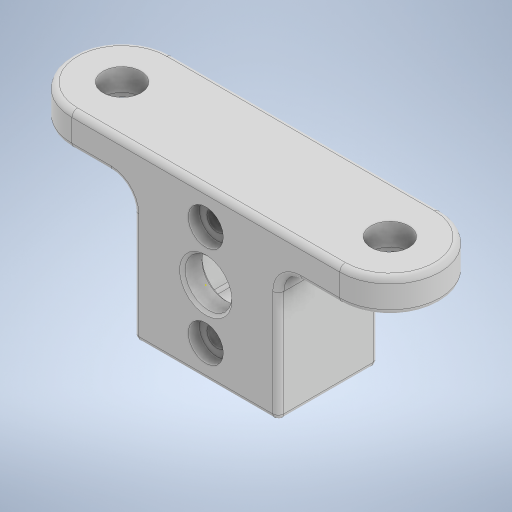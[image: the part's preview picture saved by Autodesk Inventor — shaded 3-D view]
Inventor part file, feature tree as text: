
AUTODESK INVENTOR PART (.ipt)
format: ipt  version: 2024.2 (Build 282272000, 272)  size: 382,464 bytes
history: native  units: mm
features: sketch x7, extrude x6, fillet x4, chamfer x1
ambient origin geometry x8: Origin, YZ Plane, XZ Plane, XY Plane, X Axis, Y Axis, Z Axis, Center Point
bodies: Solid1 (feature_tree)
feature tree (18):
  sketch  "Sketch1"  dims[d0=1.8mm d1=9.0mm]
  extrude  "Extrusion1"  Depth=9.0mm
  extrude  "Extrusion2"  Depth=4.5mm
  extrude  "Extrusion3"  Depth=15.0mm
  fillet  "Fillet1"  Radius=7.5mm
  fillet  "Fillet2"  Radius=6.5mm
  extrude  "Extrusion4"  Depth=1.5mm
  fillet  "Fillet3"  Radius=1.5mm
  fillet  "Fillet4"  Radius=1.5mm
  chamfer  "Chamfer1"  Distance=7.0mm
  extrude  "Extrusion5"  Depth=10.0mm
  extrude  "Extrusion6"  Depth=2.0mm
  sketch  "Sketch2"  dims[d2=4.195mm d3=4.5mm]
  sketch  "Sketch3"  dims[d4=13.0mm d5=15.0mm d6=7.5mm d7=6.5mm]
  sketch  "Sketch4"  dims[d8=2.0mm d9=0.0mm d10=1.5mm d11=1.5mm d12=1.5mm]
  sketch  "Sketch5"  dims[d13=1.5mm d14=7.0mm d15=0.0mm]
  sketch  "Sketch6"  dims[d16=3.4mm d17=10.0mm]
  sketch  "Sketch7"  dims[d18=3.0mm d19=0.0mm d20=2.0mm d21=4.5mm d22=4.5mm d23=4.5mm d24=5.25mm d25=1.0mm d26=0.0mm d27=0.5mm d28=0.25mm d29=2.0mm d30=45.0deg d31=0.25mm d32=3.15mm d33=1.0mm d34=0.0mm d35=0.2mm d36=0.0mm]
